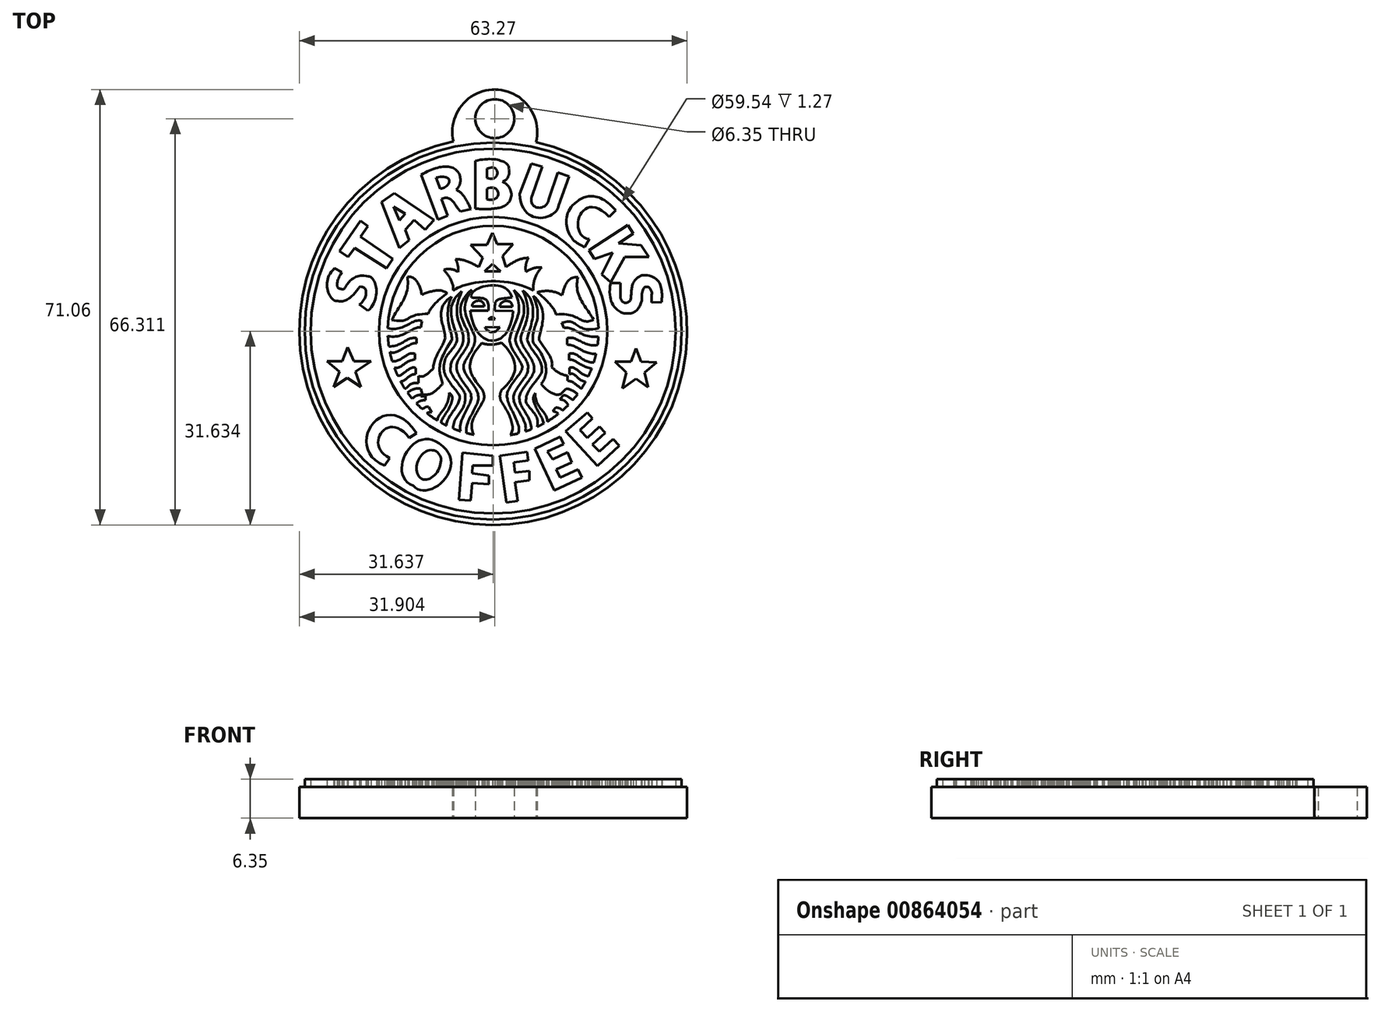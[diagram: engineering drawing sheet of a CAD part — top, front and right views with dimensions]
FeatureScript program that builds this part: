
annotation { "Feature Type Name" : "Feature", "Feature Type Description" : "" }
export const myFeature = defineFeature(function(context is Context, id is Id, definition is map)
    precondition{}
    {
        {
            var Q0;
            Q0=qCreatedBy(makeId("Top.planeOp"),FACE);
            var sketch = newSketch(context, id + "F0", { "sketchPlane" : qUnion([Q0])});
            skCircle(sketch, "E0", {"center": v(-23.32, 12.26) * mm, "radius": 31.63 * mm});
            skLineSegment(sketch, "E1", {"start": v(-49.23, 22.5) * mm, "end": v(-48.02, 21.88) * mm});
            skFitSpline(sketch, "E2", {"points": [v(-49.23, 22.5) * mm, v(-48.66, 17.2) * mm], "startDerivative": vector(-6.87, -5.81) * mm, "endDerivative": vector(4.33, 0.74) * mm});
            skFitSpline(sketch, "E3", {"points": [v(-48.66, 17.2) * mm, v(-45.1, 19.5) * mm], "startDerivative": vector(4.5, -1.36) * mm, "endDerivative": vector(2.1, 3) * mm});
            skFitSpline(sketch, "E4", {"points": [v(-45.1, 19.5) * mm, v(-45.13, 16.6) * mm], "startDerivative": vector(4.2, 0.7) * mm, "endDerivative": vector(-4.3, -3.4) * mm});
            skLineSegment(sketch, "E5", {"start": v(-45.13, 16.6) * mm, "end": v(-43.76, 15.6) * mm});
            skFitSpline(sketch, "E6", {"points": [v(-43.76, 15.6) * mm, v(-43.7, 21.17) * mm], "startDerivative": vector(7.2, 6.3) * mm, "endDerivative": vector(-3.4, -0.6) * mm});
            skFitSpline(sketch, "E7", {"points": [v(-43.7, 21.17) * mm, v(-47.7, 19.13) * mm], "startDerivative": vector(-8.2, 2.4) * mm, "endDerivative": vector(-1.1, -0.8) * mm});
            skFitSpline(sketch, "E8", {"points": [v(-47.7, 19.13) * mm, v(-48.02, 21.88) * mm], "startDerivative": vector(-3.7, -0.2) * mm, "endDerivative": vector(3.74, 6.44) * mm});
            skLineSegment(sketch, "E9", {"start": v(-45, 30.28) * mm, "end": v(-48.4, 25.33) * mm});
            skLineSegment(sketch, "E10", {"start": v(-48.4, 25.33) * mm, "end": v(-46.97, 24.36) * mm});
            skLineSegment(sketch, "E11", {"start": v(-46.97, 24.36) * mm, "end": v(-45.95, 25.84) * mm});
            skLineSegment(sketch, "E12", {"start": v(-45.95, 25.84) * mm, "end": v(-40.68, 22.54) * mm});
            skLineSegment(sketch, "E13", {"start": v(-40.68, 22.54) * mm, "end": v(-39.72, 24.08) * mm});
            skLineSegment(sketch, "E14", {"start": v(-39.72, 24.08) * mm, "end": v(-44.96, 27.68) * mm});
            skLineSegment(sketch, "E15", {"start": v(-44.96, 27.68) * mm, "end": v(-43.8, 29.38) * mm});
            skLineSegment(sketch, "E16", {"start": v(-43.8, 29.38) * mm, "end": v(-45, 30.28) * mm});
            skLineSegment(sketch, "E17", {"start": v(-41.53, 33.34) * mm, "end": v(-38.6, 25.8) * mm});
            skLineSegment(sketch, "E18", {"start": v(-38.6, 25.8) * mm, "end": v(-37.01, 27.08) * mm});
            skLineSegment(sketch, "E19", {"start": v(-37.65, 28.82) * mm, "end": v(-36.22, 30.41) * mm});
            skLineSegment(sketch, "E20", {"start": v(-36.22, 30.41) * mm, "end": v(-34.45, 28.82) * mm});
            skLineSegment(sketch, "E21", {"start": v(-34.45, 28.82) * mm, "end": v(-32.97, 30.41) * mm});
            skLineSegment(sketch, "E22", {"start": v(-32.97, 30.41) * mm, "end": v(-39.47, 34.77) * mm});
            skLineSegment(sketch, "E23", {"start": v(-39.47, 34.77) * mm, "end": v(-41.53, 33.34) * mm});
            skPoint(sketch, "E24.startSnap0", {"position": v(-36.22, 32.6) * mm});
            skLineSegment(sketch, "E25", {"start": v(-38.63, 30.33) * mm, "end": v(-39.6, 32.6) * mm});
            skLineSegment(sketch, "E26", {"start": v(-38.63, 30.33) * mm, "end": v(-37.65, 31.42) * mm});
            skLineSegment(sketch, "E27", {"start": v(-37.65, 31.42) * mm, "end": v(-39.6, 32.6) * mm});
            skLineSegment(sketch, "E28", {"start": v(-37.65, 28.82) * mm, "end": v(-37.01, 27.08) * mm});
            skLineSegment(sketch, "E29", {"start": v(-35.04, 37.8) * mm, "end": v(-32.34, 30.5) * mm});
            skLineSegment(sketch, "E30", {"start": v(-32.34, 30.5) * mm, "end": v(-30.76, 31.07) * mm});
            skLineSegment(sketch, "E31", {"start": v(-30.76, 31.07) * mm, "end": v(-31.77, 33.8) * mm});
            skLineSegment(sketch, "E32", {"start": v(-32.66, 37.31) * mm, "end": v(-31.94, 35.49) * mm});
            skFitSpline(sketch, "E33", {"points": [v(-32.66, 37.31) * mm, v(-31.94, 35.49) * mm], "startDerivative": vector(9.27, 2.15) * mm, "endDerivative": vector(-5.47, -0.96) * mm});
            skFitSpline(sketch, "E34", {"points": [v(-31.77, 33.8) * mm, v(-28.68, 31.8) * mm], "startDerivative": vector(4.9, 2.77) * mm, "endDerivative": vector(2.4, -2.4) * mm});
            skFitSpline(sketch, "E35", {"points": [v(-35.04, 37.8) * mm, v(-28.79, 37.8) * mm], "startDerivative": vector(7.44, 4.41) * mm, "endDerivative": vector(2.9, -6.2) * mm});
            skFitSpline(sketch, "E36", {"points": [v(-28.79, 37.8) * mm, v(-29.36, 35.36) * mm], "startDerivative": vector(0.8, -3.3) * mm, "endDerivative": vector(-2.1, -1.9) * mm});
            skLineSegment(sketch, "E37", {"start": v(-28.68, 31.8) * mm, "end": v(-26.96, 32.16) * mm});
            skFitSpline(sketch, "E38", {"points": [v(-26.96, 32.16) * mm, v(-29.36, 35.36) * mm], "startDerivative": vector(-1.7, 4) * mm, "endDerivative": vector(-3.5, 1.7) * mm});
            skLineSegment(sketch, "E39", {"start": v(-26.25, 40.04) * mm, "end": v(-26.25, 32.25) * mm});
            skLineSegment(sketch, "E40", {"start": v(-24.34, 38.76) * mm, "end": v(-24.34, 37.25) * mm});
            skLineSegment(sketch, "E41", {"start": v(-24.34, 35.5) * mm, "end": v(-24.34, 33.76) * mm});
            skFitSpline(sketch, "E42", {"points": [v(-24.34, 35.5) * mm, v(-24.34, 33.76) * mm], "startDerivative": vector(6.91, 2.83) * mm, "endDerivative": vector(-7.96, 1.88) * mm});
            skFitSpline(sketch, "E43", {"points": [v(-24.34, 38.76) * mm, v(-24.34, 37.25) * mm], "startDerivative": vector(6.84, 3.16) * mm, "endDerivative": vector(-6.91, 2.42) * mm});
            skFitSpline(sketch, "E44", {"points": [v(-26.25, 40.04) * mm, v(-20.75, 38.6) * mm], "startDerivative": vector(9.59, 2.4) * mm, "endDerivative": vector(-0.76, -4.03) * mm});
            skFitSpline(sketch, "E45", {"points": [v(-20.75, 38.6) * mm, v(-21.8, 36.7) * mm], "startDerivative": vector(0.6, -3.03) * mm, "endDerivative": vector(-2.03, -0.34) * mm});
            skFitSpline(sketch, "E46", {"points": [v(-21.8, 36.7) * mm, v(-22.39, 32.4) * mm], "startDerivative": vector(7.51, -4.5) * mm, "endDerivative": vector(-6, -0.8) * mm});
            skFitSpline(sketch, "E47", {"points": [v(-26.25, 32.25) * mm, v(-22.39, 32.4) * mm], "startDerivative": vector(4.38, -0.28) * mm, "endDerivative": vector(3.9, 0.8) * mm});
            skLineSegment(sketch, "E48", {"start": v(-15.3, 39.13) * mm, "end": v(-16.9, 34.55) * mm});
            skLineSegment(sketch, "E49", {"start": v(-12.75, 38.13) * mm, "end": v(-14.25, 33.85) * mm});
            skFitSpline(sketch, "E50", {"points": [v(-16.9, 34.55) * mm, v(-14.25, 33.85) * mm], "startDerivative": vector(-3.26, -7.5) * mm, "endDerivative": vector(0.73, 6.68) * mm});
            skLineSegment(sketch, "E51", {"start": v(-17.1, 39.6) * mm, "end": v(-19, 34.64) * mm});
            skLineSegment(sketch, "E52", {"start": v(-10.86, 37.62) * mm, "end": v(-12.66, 32.75) * mm});
            skFitSpline(sketch, "E53", {"points": [v(-19, 34.64) * mm, v(-12.66, 32.75) * mm], "startDerivative": vector(1, -16.93) * mm, "endDerivative": vector(0.4, 6.62) * mm});
            skLineSegment(sketch, "E54", {"start": v(-17.1, 39.6) * mm, "end": v(-15.3, 39.13) * mm});
            skLineSegment(sketch, "E55", {"start": v(-12.75, 38.13) * mm, "end": v(-10.9, 37.49) * mm});
            skLineSegment(sketch, "E56", {"start": v(-3.33, 32) * mm, "end": v(-4.37, 30.9) * mm});
            skLineSegment(sketch, "E57", {"start": v(-7.65, 27.3) * mm, "end": v(-8.42, 25.98) * mm});
            skFitSpline(sketch, "E58", {"points": [v(-3.33, 32) * mm, v(-9.68, 33.36) * mm], "startDerivative": vector(-7.07, 8.25) * mm, "endDerivative": vector(-4.71, -4.38) * mm});
            skFitSpline(sketch, "E59", {"points": [v(-9.68, 33.36) * mm, v(-9.68, 26.68) * mm], "startDerivative": vector(-8.75, -6.06) * mm, "endDerivative": vector(4.68, -2.86) * mm});
            skLineSegment(sketch, "E60", {"start": v(-9.68, 26.68) * mm, "end": v(-8.42, 25.98) * mm});
            skFitSpline(sketch, "E61", {"points": [v(-4.37, 30.9) * mm, v(-7.65, 27.3) * mm], "startDerivative": vector(-14.62, 14.86) * mm, "endDerivative": vector(10.77, -1) * mm});
            skLineSegment(sketch, "E62", {"start": v(-1.35, 29.58) * mm, "end": v(-7.68, 25.44) * mm});
            skLineSegment(sketch, "E63", {"start": v(-7.68, 25.44) * mm, "end": v(-6.78, 24.07) * mm});
            skLineSegment(sketch, "E64", {"start": v(-1.35, 29.58) * mm, "end": v(-0.44, 28.2) * mm});
            skLineSegment(sketch, "E65", {"start": v(-0.44, 28.2) * mm, "end": v(-2.87, 26.6) * mm});
            skLineSegment(sketch, "E66", {"start": v(-2.87, 26.6) * mm, "end": v(0.84, 26.3) * mm});
            skLineSegment(sketch, "E67", {"start": v(0.84, 26.3) * mm, "end": v(2.08, 24.4) * mm});
            skLineSegment(sketch, "E68", {"start": v(2.08, 24.4) * mm, "end": v(-1.86, 24.4) * mm});
            skLineSegment(sketch, "E69", {"start": v(-1.86, 24.4) * mm, "end": v(-4.15, 20.24) * mm});
            skLineSegment(sketch, "E70", {"start": v(-4.15, 20.24) * mm, "end": v(-5.6, 21.5) * mm});
            skLineSegment(sketch, "E71", {"start": v(-5.6, 21.5) * mm, "end": v(-3.81, 25.1) * mm});
            skLineSegment(sketch, "E72", {"start": v(-3.81, 25.1) * mm, "end": v(-6.78, 24.07) * mm});
            skFitSpline(sketch, "E73", {"points": [v(4.15, 16.98) * mm, v(0.96, 21.4) * mm], "startDerivative": vector(0.4, 4.2) * mm, "endDerivative": vector(-10.76, -0.62) * mm});
            skFitSpline(sketch, "E74", {"points": [v(0.96, 21.4) * mm, v(-0.93, 17.24) * mm], "startDerivative": vector(-6.23, -2.66) * mm, "endDerivative": vector(-0.96, -4.87) * mm});
            skFitSpline(sketch, "E75", {"points": [v(-0.93, 17.24) * mm, v(-2.57, 17.71) * mm], "startDerivative": vector(-2.15, -1.81) * mm, "endDerivative": vector(-0.8, 2.66) * mm});
            skLineSegment(sketch, "E76", {"start": v(-2.57, 17.71) * mm, "end": v(-2.57, 20.1) * mm});
            skLineSegment(sketch, "E77", {"start": v(-2.57, 20.1) * mm, "end": v(-4.15, 20.1) * mm});
            skFitSpline(sketch, "E78", {"points": [v(-4.15, 20.1) * mm, v(-1.47, 15.18) * mm], "startDerivative": vector(-2.44, -12.23) * mm, "endDerivative": vector(1.98, 0.74) * mm});
            skFitSpline(sketch, "E79", {"points": [v(-1.47, 15.18) * mm, v(0.94, 18.03) * mm], "startDerivative": vector(5.38, -0.85) * mm, "endDerivative": vector(-0.5, 2.89) * mm});
            skFitSpline(sketch, "E80", {"points": [v(0.94, 18.03) * mm, v(2.51, 18.03) * mm], "startDerivative": vector(0.11, 7.42) * mm, "endDerivative": vector(-1.25, -4.13) * mm});
            skLineSegment(sketch, "E81", {"start": v(2.51, 18.03) * mm, "end": v(2.51, 16.92) * mm});
            skLineSegment(sketch, "E82", {"start": v(2.51, 16.92) * mm, "end": v(4.15, 16.98) * mm});
            skLineSegment(sketch, "E83", {"start": v(0, 9.47) * mm, "end": v(-0.85, 7.3) * mm});
            skLineSegment(sketch, "E84", {"start": v(-0.85, 7.3) * mm, "end": v(-3.42, 7.3) * mm});
            skLineSegment(sketch, "E85", {"start": v(-3.42, 7.3) * mm, "end": v(-1.57, 5.48) * mm});
            skLineSegment(sketch, "E86", {"start": v(-1.57, 5.48) * mm, "end": v(-2.21, 2.93) * mm});
            skLineSegment(sketch, "E87", {"start": v(-2.21, 2.93) * mm, "end": v(0, 4.48) * mm});
            skLineSegment(sketch, "E88", {"start": v(0, 4.48) * mm, "end": v(1.98, 3.12) * mm});
            skLineSegment(sketch, "E89", {"start": v(1.98, 3.12) * mm, "end": v(1.4, 5.48) * mm});
            skLineSegment(sketch, "E90", {"start": v(1.4, 5.48) * mm, "end": v(3.36, 7.16) * mm});
            skLineSegment(sketch, "E91", {"start": v(3.36, 7.16) * mm, "end": v(0.8, 7.3) * mm});
            skLineSegment(sketch, "E92", {"start": v(0.8, 7.3) * mm, "end": v(0, 9.47) * mm});
            skLineSegment(sketch, "E93", {"start": v(-47.07, 9.66) * mm, "end": v(-47.93, 7.37) * mm});
            skLineSegment(sketch, "E94", {"start": v(-47.93, 7.37) * mm, "end": v(-50.42, 7.37) * mm});
            skLineSegment(sketch, "E95", {"start": v(-50.42, 7.37) * mm, "end": v(-48.4, 5.61) * mm});
            skLineSegment(sketch, "E96", {"start": v(-48.4, 5.61) * mm, "end": v(-49.37, 3.14) * mm});
            skLineSegment(sketch, "E97", {"start": v(-49.37, 3.14) * mm, "end": v(-47.12, 4.63) * mm});
            skLineSegment(sketch, "E98", {"start": v(-47.12, 4.63) * mm, "end": v(-44.9, 3.14) * mm});
            skLineSegment(sketch, "E99", {"start": v(-44.9, 3.14) * mm, "end": v(-45.78, 5.61) * mm});
            skLineSegment(sketch, "E100", {"start": v(-45.78, 5.61) * mm, "end": v(-43.27, 7.37) * mm});
            skLineSegment(sketch, "E101", {"start": v(-43.27, 7.37) * mm, "end": v(-46.06, 7.37) * mm});
            skLineSegment(sketch, "E102", {"start": v(-46.06, 7.37) * mm, "end": v(-47.07, 9.66) * mm});
            skFitSpline(sketch, "E103", {"points": [v(-35.8, -4.4) * mm, v(-41.04, -9.69) * mm], "startDerivative": vector(-16.2, 24.29) * mm, "endDerivative": vector(20.89, -8.4) * mm});
            skFitSpline(sketch, "E104", {"points": [v(-37.03, -5.14) * mm, v(-40.2, -8.46) * mm], "startDerivative": vector(-10.45, 14.02) * mm, "endDerivative": vector(12.95, -6.18) * mm});
            skLineSegment(sketch, "E105", {"start": v(-35.8, -4.4) * mm, "end": v(-37.03, -5.14) * mm});
            skLineSegment(sketch, "E106", {"start": v(-40.2, -8.46) * mm, "end": v(-41.04, -9.69) * mm});
            skFitSpline(sketch, "E107", {"points": [v(-32.16, -6.08) * mm, v(-36.34, -12.95) * mm], "startDerivative": vector(16.44, -10.89) * mm, "endDerivative": vector(-7.1, 9.07) * mm});
            skFitSpline(sketch, "E108", {"points": [v(-32.16, -6.08) * mm, v(-36.34, -12.95) * mm], "startDerivative": vector(-13.12, 9.58) * mm, "endDerivative": vector(13.48, -4.94) * mm});
            skFitSpline(sketch, "E109", {"points": [v(-32.66, -7.32) * mm, v(-35.23, -11.65) * mm], "startDerivative": vector(6.85, -4.03) * mm, "endDerivative": vector(-5.66, 4.74) * mm});
            skFitSpline(sketch, "E110", {"points": [v(-32.66, -7.32) * mm, v(-35.23, -11.65) * mm], "startDerivative": vector(-6.44, 3.03) * mm, "endDerivative": vector(5.06, -4.74) * mm});
            skLineSegment(sketch, "E111", {"start": v(-28.34, -7.57) * mm, "end": v(-28.87, -15.27) * mm});
            skLineSegment(sketch, "E112", {"start": v(-28.87, -15.27) * mm, "end": v(-26.97, -15.4) * mm});
            skLineSegment(sketch, "E113", {"start": v(-26.97, -15.4) * mm, "end": v(-26.77, -12.53) * mm});
            skLineSegment(sketch, "E114", {"start": v(-26.77, -12.53) * mm, "end": v(-23.98, -12.72) * mm});
            skLineSegment(sketch, "E115", {"start": v(-23.98, -12.72) * mm, "end": v(-23.98, -11.3) * mm});
            skLineSegment(sketch, "E116", {"start": v(-23.98, -11.3) * mm, "end": v(-26.77, -10.94) * mm});
            skLineSegment(sketch, "E117", {"start": v(-26.77, -10.94) * mm, "end": v(-26.68, -9.63) * mm});
            skLineSegment(sketch, "E118", {"start": v(-26.68, -9.63) * mm, "end": v(-23.38, -9.63) * mm});
            skLineSegment(sketch, "E119", {"start": v(-23.38, -9.63) * mm, "end": v(-23.38, -8.1) * mm});
            skLineSegment(sketch, "E120", {"start": v(-23.38, -8.1) * mm, "end": v(-28.34, -7.57) * mm});
            skLineSegment(sketch, "E121", {"start": v(-22.26, -8.06) * mm, "end": v(-21.15, -15.71) * mm});
            skLineSegment(sketch, "E122", {"start": v(-21.15, -15.71) * mm, "end": v(-19.3, -15.45) * mm});
            skLineSegment(sketch, "E123", {"start": v(-19.3, -15.45) * mm, "end": v(-19.74, -12.4) * mm});
            skLineSegment(sketch, "E124", {"start": v(-19.74, -12.4) * mm, "end": v(-17.42, -12.06) * mm});
            skLineSegment(sketch, "E125", {"start": v(-17.42, -12.06) * mm, "end": v(-17.42, -10.52) * mm});
            skLineSegment(sketch, "E126", {"start": v(-17.42, -10.52) * mm, "end": v(-19.74, -10.83) * mm});
            skLineSegment(sketch, "E127", {"start": v(-19.74, -10.83) * mm, "end": v(-19.96, -9.17) * mm});
            skLineSegment(sketch, "E128", {"start": v(-19.96, -9.17) * mm, "end": v(-17.61, -8.86) * mm});
            skLineSegment(sketch, "E129", {"start": v(-17.61, -8.86) * mm, "end": v(-17.8, -7.41) * mm});
            skLineSegment(sketch, "E130", {"start": v(-17.8, -7.41) * mm, "end": v(-22.26, -8.06) * mm});
            skLineSegment(sketch, "E131", {"start": v(-16.54, -6.93) * mm, "end": v(-13.37, -13.75) * mm});
            skLineSegment(sketch, "E132", {"start": v(-13.37, -13.75) * mm, "end": v(-8.86, -11.66) * mm});
            skLineSegment(sketch, "E133", {"start": v(-8.86, -11.66) * mm, "end": v(-9.48, -10.31) * mm});
            skLineSegment(sketch, "E134", {"start": v(-9.48, -10.31) * mm, "end": v(-12.39, -11.66) * mm});
            skLineSegment(sketch, "E135", {"start": v(-12.39, -11.66) * mm, "end": v(-13.01, -10.31) * mm});
            skLineSegment(sketch, "E136", {"start": v(-13.01, -10.31) * mm, "end": v(-10.46, -9.13) * mm});
            skLineSegment(sketch, "E137", {"start": v(-10.46, -9.13) * mm, "end": v(-11.2, -7.53) * mm});
            skLineSegment(sketch, "E138", {"start": v(-11.2, -7.53) * mm, "end": v(-13.62, -8.65) * mm});
            skLineSegment(sketch, "E139", {"start": v(-16.54, -6.93) * mm, "end": v(-12.36, -5) * mm});
            skLineSegment(sketch, "E140", {"start": v(-12.36, -5) * mm, "end": v(-11.82, -6.15) * mm});
            skLineSegment(sketch, "E141", {"start": v(-11.82, -6.15) * mm, "end": v(-14.46, -7.38) * mm});
            skLineSegment(sketch, "E142", {"start": v(-14.46, -7.38) * mm, "end": v(-13.62, -8.65) * mm});
            skLineSegment(sketch, "E143", {"start": v(-11.5, -4.1) * mm, "end": v(-6.3, -9.72) * mm});
            skLineSegment(sketch, "E144", {"start": v(-6.3, -9.72) * mm, "end": v(-2.73, -6.42) * mm});
            skLineSegment(sketch, "E145", {"start": v(-2.73, -6.42) * mm, "end": v(-3.74, -5.32) * mm});
            skLineSegment(sketch, "E146", {"start": v(-3.74, -5.32) * mm, "end": v(-6, -7.4) * mm});
            skLineSegment(sketch, "E147", {"start": v(-6, -7.4) * mm, "end": v(-7.1, -6.22) * mm});
            skLineSegment(sketch, "E148", {"start": v(-7.1, -6.22) * mm, "end": v(-5.05, -4.34) * mm});
            skLineSegment(sketch, "E149", {"start": v(-5.05, -4.34) * mm, "end": v(-6, -3.3) * mm});
            skLineSegment(sketch, "E150", {"start": v(-6, -3.3) * mm, "end": v(-7.98, -5.13) * mm});
            skLineSegment(sketch, "E151", {"start": v(-7.98, -5.13) * mm, "end": v(-9.13, -3.89) * mm});
            skLineSegment(sketch, "E152", {"start": v(-9.13, -3.89) * mm, "end": v(-7.1, -2) * mm});
            skLineSegment(sketch, "E153", {"start": v(-7.1, -2) * mm, "end": v(-7.98, -1.05) * mm});
            skLineSegment(sketch, "E154", {"start": v(-7.98, -1.05) * mm, "end": v(-11.5, -4.1) * mm});
            skLineSegment(sketch, "E155", {"start": v(-23.47, 28.32) * mm, "end": v(-22.68, 26.44) * mm});
            skLineSegment(sketch, "E156", {"start": v(-22.68, 26.44) * mm, "end": v(-20.07, 26.44) * mm});
            skLineSegment(sketch, "E157", {"start": v(-20.07, 26.44) * mm, "end": v(-21.78, 24.48) * mm});
            skLineSegment(sketch, "E158", {"start": v(-21.78, 24.48) * mm, "end": v(-21.23, 22.74) * mm});
            skLineSegment(sketch, "E159", {"start": v(-23.47, 23.2) * mm, "end": v(-22.09, 22.02) * mm});
            skLineSegment(sketch, "E160", {"start": v(-23.47, 23.2) * mm, "end": v(-24.72, 22.02) * mm});
            skLineSegment(sketch, "E161", {"start": v(-24.72, 22.02) * mm, "end": v(-22.09, 22.02) * mm});
            skLineSegment(sketch, "E162", {"start": v(-23.47, 28.32) * mm, "end": v(-24.3, 26.35) * mm});
            skLineSegment(sketch, "E163", {"start": v(-24.3, 26.35) * mm, "end": v(-26.99, 26.35) * mm});
            skLineSegment(sketch, "E164", {"start": v(-26.99, 26.35) * mm, "end": v(-25, 24.26) * mm});
            skLineSegment(sketch, "E165", {"start": v(-25, 24.26) * mm, "end": v(-25.67, 22.72) * mm});
            skFitSpline(sketch, "E166", {"points": [v(-29.83, 18.82) * mm, v(-16.77, 18.9) * mm], "startDerivative": vector(3.6, 3.92) * mm, "endDerivative": vector(14.42, -8.07) * mm});
            skFitSpline(sketch, "E167", {"points": [v(-31.37, 22.26) * mm, v(-29.83, 18.82) * mm], "startDerivative": vector(2.43, -2.5) * mm, "endDerivative": vector(-0.31, -4.08) * mm});
            skFitSpline(sketch, "E168", {"points": [v(-31.37, 22.26) * mm, v(-29.02, 21.92) * mm], "startDerivative": vector(1.49, 0.78) * mm, "endDerivative": vector(2.35, -1.57) * mm});
            skFitSpline(sketch, "E169", {"points": [v(-29.46, 24.01) * mm, v(-29.02, 21.92) * mm], "startDerivative": vector(0.94, -1.65) * mm, "endDerivative": vector(-0.16, -2.12) * mm});
            skFitSpline(sketch, "E170", {"points": [v(-29.46, 24.01) * mm, v(-25.67, 22.72) * mm], "startDerivative": vector(3.84, 0.08) * mm, "endDerivative": vector(3.7, -2.15) * mm});
            skFitSpline(sketch, "E171", {"points": [v(-16.77, 18.9) * mm, v(-15.4, 22.65) * mm], "startDerivative": vector(-0.2, 4.33) * mm, "endDerivative": vector(3.1, 3.33) * mm});
            skFitSpline(sketch, "E172", {"points": [v(-15.4, 22.65) * mm, v(-17.96, 21.96) * mm], "startDerivative": vector(-2.94, 0.22) * mm, "endDerivative": vector(-2.44, -1.55) * mm});
            skFitSpline(sketch, "E173", {"points": [v(-17.96, 21.96) * mm, v(-17.53, 24.22) * mm], "startDerivative": vector(-0.6, 2.66) * mm, "endDerivative": vector(0.94, 1.22) * mm});
            skFitSpline(sketch, "E174", {"points": [v(-21.23, 22.74) * mm, v(-17.53, 24.22) * mm], "startDerivative": vector(3.33, 2.09) * mm, "endDerivative": vector(4.54, 0) * mm});
            skFitSpline(sketch, "E175", {"points": [v(-26.9, 17.8) * mm, v(-20.26, 17.75) * mm], "startDerivative": vector(-0.96, 5.66) * mm, "endDerivative": vector(2.07, -9.89) * mm});
            skFitSpline(sketch, "E176", {"points": [v(-26.9, 17.8) * mm, v(-24.11, 15.61) * mm], "startDerivative": vector(3.9, -1.04) * mm, "endDerivative": vector(-0.88, -8.21) * mm});
            skFitSpline(sketch, "E177", {"points": [v(-24.67, 12.9) * mm, v(-22.25, 12.93) * mm], "startDerivative": vector(0.79, -1.9) * mm, "endDerivative": vector(2.57, 4.41) * mm});
            skLineSegment(sketch, "E178", {"start": v(-24.67, 12.9) * mm, "end": v(-22.25, 12.93) * mm});
            skLineSegment(sketch, "E179", {"start": v(-24.08, 14.18) * mm, "end": v(-23.01, 14.18) * mm});
            skFitSpline(sketch, "E180", {"points": [v(-24.08, 14.18) * mm, v(-23.01, 14.18) * mm], "startDerivative": vector(1.05, 1.37) * mm, "endDerivative": vector(0.9, -1.58) * mm});
            skFitSpline(sketch, "E181", {"points": [v(-27.04, 15.6) * mm, v(-20.08, 15.57) * mm], "startDerivative": vector(1.96, -19.15) * mm, "endDerivative": vector(1.4, 20.06) * mm});
            skLineSegment(sketch, "E182", {"start": v(-27.04, 15.6) * mm, "end": v(-24.11, 15.61) * mm});
            skFitSpline(sketch, "E183", {"points": [v(-20.26, 17.75) * mm, v(-23.08, 15.6) * mm], "startDerivative": vector(-8.3, -0.7) * mm, "endDerivative": vector(-0.17, -5.73) * mm});
            skLineSegment(sketch, "E184", {"start": v(-20.08, 15.57) * mm, "end": v(-23.08, 15.6) * mm});
            skFitSpline(sketch, "E185", {"points": [v(-22.22, 16.25) * mm, v(-20.18, 16.22) * mm], "startDerivative": vector(-0.62, 2.67) * mm, "endDerivative": vector(0.3, -4.87) * mm});
            skFitSpline(sketch, "E186", {"points": [v(-21.49, 16.25) * mm, v(-20.84, 16.22) * mm], "startDerivative": vector(0.05, 1.2) * mm, "endDerivative": vector(0.25, -1.82) * mm});
            skLineSegment(sketch, "E187", {"start": v(-22.22, 16.25) * mm, "end": v(-20.18, 16.22) * mm});
            skFitSpline(sketch, "E188", {"points": [v(-26.76, 16.3) * mm, v(-24.76, 16.3) * mm], "startDerivative": vector(-0.34, 3.08) * mm, "endDerivative": vector(0.14, -4.37) * mm});
            skFitSpline(sketch, "E189", {"points": [v(-26.08, 16.3) * mm, v(-25.29, 16.29) * mm], "startDerivative": vector(0.2, 1.39) * mm, "endDerivative": vector(0.4, -1.53) * mm});
            skLineSegment(sketch, "E190", {"start": v(-26.76, 16.3) * mm, "end": v(-24.76, 16.3) * mm});
            skFitSpline(sketch, "E191", {"points": [v(-25.15, 10.33) * mm, v(-21.97, 10.37) * mm], "startDerivative": vector(2.7, -1.14) * mm, "endDerivative": vector(3.03, 1.08) * mm});
            skFitSpline(sketch, "E192", {"points": [v(-21.97, 10.37) * mm, v(-21.97, 2.63) * mm], "startDerivative": vector(10.1, -9.77) * mm, "endDerivative": vector(-7.54, -6.67) * mm});
            skFitSpline(sketch, "E193", {"points": [v(-25.15, 10.33) * mm, v(-25.15, 2.79) * mm], "startDerivative": vector(-9.36, -10.5) * mm, "endDerivative": vector(6.06, -7.48) * mm});
            skFitSpline(sketch, "E194", {"points": [v(-25.15, 2.79) * mm, v(-25.15, 0.54) * mm], "startDerivative": vector(1.3, -2.11) * mm, "endDerivative": vector(-1.6, -1.9) * mm});
            skFitSpline(sketch, "E195", {"points": [v(-21.97, 2.63) * mm, v(-21.97, 0.73) * mm], "startDerivative": vector(-0.92, -1.93) * mm, "endDerivative": vector(1.02, -1.86) * mm});
            skFitSpline(sketch, "E196", {"points": [v(-25.15, 0.54) * mm, v(-26.48, -4.64) * mm], "startDerivative": vector(-3.25, -6.67) * mm, "endDerivative": vector(2.78, -6.34) * mm});
            skFitSpline(sketch, "E197", {"points": [v(-21.97, 0.73) * mm, v(-20.53, -4.7) * mm], "startDerivative": vector(3.67, -5.26) * mm, "endDerivative": vector(-3, -3.62) * mm});
            skFitSpline(sketch, "E198", {"points": [v(-37.3, 21.13) * mm, v(-39.87, 14.07) * mm], "startDerivative": vector(1.47, -9.46) * mm, "endDerivative": vector(-3.23, -6.85) * mm});
            skFitSpline(sketch, "E199", {"points": [v(-37.3, 21.13) * mm, v(-34.94, 18.24) * mm], "startDerivative": vector(4.3, 0.45) * mm, "endDerivative": vector(0.96, -4.3) * mm});
            skFitSpline(sketch, "E200", {"points": [v(-34.94, 18.24) * mm, v(-30.82, 18.46) * mm], "startDerivative": vector(4.64, 1.53) * mm, "endDerivative": vector(3.74, -2.72) * mm});
            skFitSpline(sketch, "E201", {"points": [v(-30.82, 18.46) * mm, v(-33.95, 15.09) * mm], "startDerivative": vector(-3.75, -2.78) * mm, "endDerivative": vector(-1.86, -4.12) * mm});
            skFitSpline(sketch, "E202", {"points": [v(-39.87, 14.07) * mm, v(-33.95, 15.09) * mm], "startDerivative": vector(10.28, -1.75) * mm, "endDerivative": vector(12.35, 0.11) * mm});
            skCircle(sketch, "E203", {"center": v(-23.32, 12.26) * mm, "radius": 18.62 * mm});
            skCircle(sketch, "E204", {"center": v(-23.32, 12.26) * mm, "radius": 17.2 * mm});
            skCircle(sketch, "E205", {"center": v(-23.32, 12.26) * mm, "radius": 30.76 * mm});
            skCircle(sketch, "E206", {"center": v(-23.32, 12.26) * mm, "radius": 29.77 * mm});
            skFitSpline(sketch, "E207", {"points": [v(-9.48, 21.06) * mm, v(-6.95, 14.16) * mm], "startDerivative": vector(-2.38, -8.84) * mm, "endDerivative": vector(3.62, -6.46) * mm});
            skFitSpline(sketch, "E208", {"points": [v(-9.48, 21.06) * mm, v(-12.09, 18.12) * mm], "startDerivative": vector(-6.23, 0.45) * mm, "endDerivative": vector(-1.13, -2.72) * mm});
            skFitSpline(sketch, "E209", {"points": [v(-16.12, 18.6) * mm, v(-12.09, 18.12) * mm], "startDerivative": vector(4.3, 1.25) * mm, "endDerivative": vector(3.51, -2.27) * mm});
            skFitSpline(sketch, "E210", {"points": [v(-16.12, 18.6) * mm, v(-13.06, 15) * mm], "startDerivative": vector(3.62, -2.83) * mm, "endDerivative": vector(0.45, -3.06) * mm});
            skFitSpline(sketch, "E211", {"points": [v(-13.06, 15) * mm, v(-6.95, 14.16) * mm], "startDerivative": vector(11.75, 1.2) * mm, "endDerivative": vector(6.07, 3.47) * mm});
            skFitSpline(sketch, "E212", {"points": [v(-34.93, 13.92) * mm, v(-40.5, 12.74) * mm], "startDerivative": vector(-4.63, 1.77) * mm, "endDerivative": vector(-7.71, 2.16) * mm});
            skLineSegment(sketch, "E213", {"start": v(-34.93, 13.92) * mm, "end": v(-35.15, 12.85) * mm});
            skFitSpline(sketch, "E214", {"points": [v(-35.15, 12.85) * mm, v(-40.5, 11.46) * mm], "startDerivative": vector(-3.32, 1.22) * mm, "endDerivative": vector(-7.72, 1.76) * mm});
            skFitSpline(sketch, "E215", {"points": [v(-35.8, 11.13) * mm, v(-40.33, 9.78) * mm], "startDerivative": vector(-5.26, 0.92) * mm, "endDerivative": vector(-7.25, -0.07) * mm});
            skLineSegment(sketch, "E216", {"start": v(-35.8, 11.13) * mm, "end": v(-35.8, 10.25) * mm});
            skFitSpline(sketch, "E217", {"points": [v(-35.8, 10.25) * mm, v(-40.17, 8.85) * mm], "startDerivative": vector(-2.2, 1.43) * mm, "endDerivative": vector(-3, 1.94) * mm});
            skLineSegment(sketch, "E218", {"start": v(-36.08, 8.57) * mm, "end": v(-36.08, 7.68) * mm});
            skFitSpline(sketch, "E219", {"points": [v(-36.08, 8.57) * mm, v(-39.8, 7.37) * mm], "startDerivative": vector(-3.58, 1.5) * mm, "endDerivative": vector(-4.24, 0.85) * mm});
            skFitSpline(sketch, "E220", {"points": [v(-36.08, 7.68) * mm, v(-39.43, 6.26) * mm], "startDerivative": vector(-5.93, -1.2) * mm, "endDerivative": vector(-4.56, 0.07) * mm});
            skLineSegment(sketch, "E221", {"start": v(-35.97, 6.22) * mm, "end": v(-35.97, 5.25) * mm});
            skFitSpline(sketch, "E222", {"points": [v(-35.97, 6.22) * mm, v(-38.92, 5.03) * mm], "startDerivative": vector(-2.6, 1.88) * mm, "endDerivative": vector(-1.78, 1.2) * mm});
            skFitSpline(sketch, "E223", {"points": [v(-35.97, 5.25) * mm, v(-38.44, 4.08) * mm], "startDerivative": vector(-3.93, -0.1) * mm, "endDerivative": vector(-2.76, 0.24) * mm});
            skFitSpline(sketch, "E224", {"points": [v(-35.51, 3.8) * mm, v(-37.75, 2.92) * mm], "startDerivative": vector(-5.28, 0.6) * mm, "endDerivative": vector(-1.62, 0.34) * mm});
            skFitSpline(sketch, "E225", {"points": [v(-35.11, 2.83) * mm, v(-37.26, 2.2) * mm], "startDerivative": vector(-1.97, 0.82) * mm, "endDerivative": vector(-1, -1.35) * mm});
            skLineSegment(sketch, "E226", {"start": v(-35.11, 2.83) * mm, "end": v(-34.88, 1.94) * mm});
            skFitSpline(sketch, "E227", {"points": [v(-34.88, 1.94) * mm, v(-31.55, 3.65) * mm], "startDerivative": vector(5.15, -1.1) * mm, "endDerivative": vector(2.57, 2.15) * mm});
            skLineSegment(sketch, "E228", {"start": v(-35.51, 3.8) * mm, "end": v(-35.51, 4.94) * mm});
            skFitSpline(sketch, "E229", {"points": [v(-35.51, 4.94) * mm, v(-33.06, 6.13) * mm], "startDerivative": vector(3.94, -1.13) * mm, "endDerivative": vector(2.03, 0.84) * mm});
            skFitSpline(sketch, "E230", {"points": [v(-33.06, 6.13) * mm, v(-31.14, 11.16) * mm], "startDerivative": vector(-0.5, 5.04) * mm, "endDerivative": vector(0.7, 3.82) * mm});
            skFitSpline(sketch, "E231", {"points": [v(-31.14, 11.16) * mm, v(-30.14, 17.92) * mm], "startDerivative": vector(-0.12, 6.25) * mm, "endDerivative": vector(9.14, 6.37) * mm});
            skFitSpline(sketch, "E232", {"points": [v(-31.55, 3.65) * mm, v(-30.16, 10.63) * mm], "startDerivative": vector(-1.63, 6.08) * mm, "endDerivative": vector(7.98, 12.11) * mm});
            skFitSpline(sketch, "E233", {"points": [v(-30.16, 10.63) * mm, v(-30.14, 17.92) * mm], "startDerivative": vector(1.93, 2.34) * mm, "endDerivative": vector(4.74, 11.4) * mm});
            skLineSegment(sketch, "E234", {"start": v(-35.1, 1.9) * mm, "end": v(-35.1, 1.63) * mm});
            skLineSegment(sketch, "E235", {"start": v(-35.1, 1.63) * mm, "end": v(-34.35, 1.63) * mm});
            skLineSegment(sketch, "E236", {"start": v(-34.35, 1.63) * mm, "end": v(-34.35, 1.02) * mm});
            skFitSpline(sketch, "E237", {"points": [v(-34.35, 1.02) * mm, v(-35.84, 0.48) * mm], "startDerivative": vector(-3.5, -0.24) * mm, "endDerivative": vector(-0.96, -0.52) * mm});
            skFitSpline(sketch, "E238", {"points": [v(-35.1, 1.9) * mm, v(-36.5, 1.23) * mm], "startDerivative": vector(-1.5, -0.05) * mm, "endDerivative": vector(-1.12, -1.26) * mm});
            skFitSpline(sketch, "E239", {"points": [v(-33.87, -0.05) * mm, v(-34.95, -0.4) * mm], "startDerivative": vector(-1.69, 0.16) * mm, "endDerivative": vector(-1.56, -0.23) * mm});
            skLineSegment(sketch, "E240.bottom", {"start": v(-33.87, -0.05) * mm, "end": v(-33.95, -0.1) * mm});
            skLineSegment(sketch, "E241", {"start": v(-33.87, -0.05) * mm, "end": v(-33.36, -0.95) * mm});
            skFitSpline(sketch, "E242", {"points": [v(-33.36, -0.95) * mm, v(-34.11, -1.12) * mm], "startDerivative": vector(-0.52, -0.07) * mm, "endDerivative": vector(-0.08, -0.42) * mm});
            skFitSpline(sketch, "E243", {"points": [v(-30.48, 2.2) * mm, v(-32.4, -2.33) * mm], "startDerivative": vector(-0.4, -8.5) * mm, "endDerivative": vector(0.1, -3.7) * mm});
            skFitSpline(sketch, "E244", {"points": [v(-30.48, 2.2) * mm, v(-31.75, -2.72) * mm], "startDerivative": vector(5.27, -3.57) * mm, "endDerivative": vector(1.41, -1.58) * mm});
            skLineSegment(sketch, "E245", {"start": v(-12.11, 13.62) * mm, "end": v(-11.75, 12.76) * mm});
            skFitSpline(sketch, "E246", {"points": [v(-12.11, 13.62) * mm, v(-6.14, 12.75) * mm], "startDerivative": vector(7.88, 3.03) * mm, "endDerivative": vector(11.38, 2.91) * mm});
            skFitSpline(sketch, "E247", {"points": [v(-11.75, 12.76) * mm, v(-6.16, 11.34) * mm], "startDerivative": vector(5.46, 1.08) * mm, "endDerivative": vector(9.44, 0.65) * mm});
            skFitSpline(sketch, "E248", {"points": [v(-11.26, 11.1) * mm, v(-6.28, 10) * mm], "startDerivative": vector(4.31, 1.62) * mm, "endDerivative": vector(6.3, 1.36) * mm});
            skLineSegment(sketch, "E249", {"start": v(-11.26, 11.1) * mm, "end": v(-11.26, 10.07) * mm});
            skFitSpline(sketch, "E250", {"points": [v(-11.26, 10.07) * mm, v(-6.54, 8.53) * mm], "startDerivative": vector(6.26, -0.67) * mm, "endDerivative": vector(7.41, -0.3) * mm});
            skLineSegment(sketch, "E251", {"start": v(-10.94, 8.54) * mm, "end": v(-10.94, 7.55) * mm});
            skFitSpline(sketch, "E252", {"points": [v(-10.94, 8.54) * mm, v(-6.9, 7.2) * mm], "startDerivative": vector(4.45, 1.58) * mm, "endDerivative": vector(5.92, 0.7) * mm});
            skFitSpline(sketch, "E253", {"points": [v(-10.94, 7.55) * mm, v(-7.25, 6.17) * mm], "startDerivative": vector(2.2, 1.2) * mm, "endDerivative": vector(5.41, -0.72) * mm});
            skLineSegment(sketch, "E254", {"start": v(-10.84, 6.28) * mm, "end": v(-10.84, 5.26) * mm});
            skFitSpline(sketch, "E255", {"points": [v(-10.84, 6.28) * mm, v(-7.79, 4.9) * mm], "startDerivative": vector(3.33, 1.16) * mm, "endDerivative": vector(4.27, -0.5) * mm});
            skFitSpline(sketch, "E256", {"points": [v(-10.84, 5.26) * mm, v(-8.25, 4) * mm], "startDerivative": vector(3.13, 0.88) * mm, "endDerivative": vector(4.71, -1.14) * mm});
            skFitSpline(sketch, "E257", {"points": [v(-8.9, 2.92) * mm, v(-11.18, 4.18) * mm], "startDerivative": vector(-1.1, 0.2) * mm, "endDerivative": vector(-2.89, 0.1) * mm});
            skLineSegment(sketch, "E258", {"start": v(-11.18, 4.18) * mm, "end": v(-11.18, 4.98) * mm});
            skFitSpline(sketch, "E259", {"points": [v(-11.18, 4.98) * mm, v(-13.8, 6.42) * mm], "startDerivative": vector(-3.94, 0.77) * mm, "endDerivative": vector(-2.21, 2.02) * mm});
            skFitSpline(sketch, "E260", {"points": [v(-13.8, 6.42) * mm, v(-15.77, 10.7) * mm], "startDerivative": vector(1.7, 3.41) * mm, "endDerivative": vector(-2.72, 4.37) * mm});
            skFitSpline(sketch, "E261", {"points": [v(-15.77, 10.7) * mm, v(-16.79, 18.03) * mm], "startDerivative": vector(-1.18, 3.07) * mm, "endDerivative": vector(-9.33, 8.15) * mm});
            skFitSpline(sketch, "E262", {"points": [v(-16.79, 18.03) * mm, v(-16.79, 10.32) * mm], "startDerivative": vector(5.79, -12.52) * mm, "endDerivative": vector(1.65, -8.62) * mm});
            skFitSpline(sketch, "E263", {"points": [v(-16.79, 10.32) * mm, v(-15.49, 3.7) * mm], "startDerivative": vector(7.32, -7.56) * mm, "endDerivative": vector(-3.9, -3.9) * mm});
            skFitSpline(sketch, "E264", {"points": [v(-15.49, 3.7) * mm, v(-12.26, 2.05) * mm], "startDerivative": vector(1.89, -2.95) * mm, "endDerivative": vector(2.36, 1.89) * mm});
            skLineSegment(sketch, "E265", {"start": v(-12.26, 2.05) * mm, "end": v(-11.6, 2.72) * mm});
            skFitSpline(sketch, "E266", {"points": [v(-11.6, 2.72) * mm, v(-9.55, 1.97) * mm], "startDerivative": vector(1.18, 1.54) * mm, "endDerivative": vector(1.16, -0.93) * mm});
            skLineSegment(sketch, "E267", {"start": v(-12.45, 1.16) * mm, "end": v(-11.82, 1.84) * mm});
            skFitSpline(sketch, "E268", {"points": [v(-11.82, 1.84) * mm, v(-10.34, 1) * mm], "startDerivative": vector(1.69, -0.3) * mm, "endDerivative": vector(1.08, -1.07) * mm});
            skFitSpline(sketch, "E269", {"points": [v(-12.45, 1.16) * mm, v(-11.08, 0.2) * mm], "startDerivative": vector(2.63, -0.35) * mm, "endDerivative": vector(0.58, -1.11) * mm});
            skLineSegment(sketch, "E270", {"start": v(-13.06, -0.22) * mm, "end": v(-13.6, -0.76) * mm});
            skFitSpline(sketch, "E271", {"points": [v(-13.06, -0.22) * mm, v(-12.07, -0.73) * mm], "startDerivative": vector(1.54, 0) * mm, "endDerivative": vector(0.2, -0.96) * mm});
            skFitSpline(sketch, "E272", {"points": [v(-13.6, -0.76) * mm, v(-12.69, -1.24) * mm], "startDerivative": vector(1.14, -0.5) * mm, "endDerivative": vector(0.74, -0.9) * mm});
            skFitSpline(sketch, "E273", {"points": [v(-16.44, 2.13) * mm, v(-14.5, -2.49) * mm], "startDerivative": vector(-0.65, -6.4) * mm, "endDerivative": vector(-0.62, -4.04) * mm});
            skFitSpline(sketch, "E274", {"points": [v(-16.44, 2.13) * mm, v(-15.09, -2.83) * mm], "startDerivative": vector(-3.48, -4.07) * mm, "endDerivative": vector(0.4, -4.45) * mm});
            skFitSpline(sketch, "E275", {"points": [v(-16.16, -3.36) * mm, v(-17.94, 1.21) * mm], "startDerivative": vector(2.09, 6.74) * mm, "endDerivative": vector(1.47, 3.64) * mm});
            skFitSpline(sketch, "E276", {"points": [v(-17.94, 1.21) * mm, v(-15.38, 5.9) * mm], "startDerivative": vector(-0.09, 4.92) * mm, "endDerivative": vector(-0.43, 2.94) * mm});
            skFitSpline(sketch, "E277", {"points": [v(-15.38, 5.9) * mm, v(-17.8, 10.87) * mm], "startDerivative": vector(0.02, 6.48) * mm, "endDerivative": vector(-2.67, 7.08) * mm});
            skFitSpline(sketch, "E278", {"points": [v(-17.8, 10.87) * mm, v(-18.48, 18.9) * mm], "startDerivative": vector(1.23, 5.75) * mm, "endDerivative": vector(-9.14, 6.57) * mm});
            skFitSpline(sketch, "E279", {"points": [v(-18.48, 18.9) * mm, v(-18.8, 10.94) * mm], "startDerivative": vector(6.16, -13.04) * mm, "endDerivative": vector(0.41, -4.61) * mm});
            skFitSpline(sketch, "E280", {"points": [v(-18.8, 10.94) * mm, v(-16.65, 5.88) * mm], "startDerivative": vector(-0.14, -3.87) * mm, "endDerivative": vector(-1.03, -4.93) * mm});
            skFitSpline(sketch, "E281", {"points": [v(-16.65, 5.88) * mm, v(-19.05, 1.26) * mm], "startDerivative": vector(-0.2, -3.7) * mm, "endDerivative": vector(0.62, -3.6) * mm});
            skFitSpline(sketch, "E282", {"points": [v(-19.05, 1.26) * mm, v(-17.07, -3.75) * mm], "startDerivative": vector(0.3, -5.34) * mm, "endDerivative": vector(0.48, -7.34) * mm});
            skFitSpline(sketch, "E283", {"points": [v(-18.05, -4.1) * mm, v(-20, 1.42) * mm], "startDerivative": vector(1.25, 5.84) * mm, "endDerivative": vector(0.43, 4.25) * mm});
            skFitSpline(sketch, "E284", {"points": [v(-20, 1.42) * mm, v(-17.67, 6.08) * mm], "startDerivative": vector(0, 4.66) * mm, "endDerivative": vector(-0.35, 3.97) * mm});
            skFitSpline(sketch, "E285", {"points": [v(-17.67, 6.08) * mm, v(-19.7, 10.96) * mm], "startDerivative": vector(1.51, 3.93) * mm, "endDerivative": vector(0, 5.1) * mm});
            skFitSpline(sketch, "E286", {"points": [v(-19.7, 10.96) * mm, v(-19.97, 18.96) * mm], "startDerivative": vector(0.62, 5.58) * mm, "endDerivative": vector(-10.6, 8.2) * mm});
            skFitSpline(sketch, "E287", {"points": [v(-19.97, 18.96) * mm, v(-20.6, 11.1) * mm], "startDerivative": vector(6.32, -10.6) * mm, "endDerivative": vector(-1.3, -7.26) * mm});
            skFitSpline(sketch, "E288", {"points": [v(-20.6, 11.1) * mm, v(-18.6, 6.2) * mm], "startDerivative": vector(-1.08, -4.6) * mm, "endDerivative": vector(-0.94, -2.77) * mm});
            skFitSpline(sketch, "E289", {"points": [v(-18.6, 6.2) * mm, v(-21.02, 1.4) * mm], "startDerivative": vector(-0.53, -3.2) * mm, "endDerivative": vector(1.47, -4.23) * mm});
            skFitSpline(sketch, "E290", {"points": [v(-21.02, 1.4) * mm, v(-19.24, -4.44) * mm], "startDerivative": vector(0.3, -4.17) * mm, "endDerivative": vector(-2.23, -3.71) * mm});
            skFitSpline(sketch, "E291", {"points": [v(-30.93, -3.15) * mm, v(-28.8, 1.45) * mm], "startDerivative": vector(-0.48, 4.07) * mm, "endDerivative": vector(-0.1, 4.36) * mm});
            skFitSpline(sketch, "E292", {"points": [v(-28.8, 1.45) * mm, v(-31.36, 6.35) * mm], "startDerivative": vector(0.82, 1.95) * mm, "endDerivative": vector(0.62, 5.75) * mm});
            skFitSpline(sketch, "E293", {"points": [v(-31.36, 6.35) * mm, v(-29.27, 11.35) * mm], "startDerivative": vector(-0.33, 7.6) * mm, "endDerivative": vector(-1.38, 5.37) * mm});
            skFitSpline(sketch, "E294", {"points": [v(-29.27, 11.35) * mm, v(-28.43, 18.76) * mm], "startDerivative": vector(-0.61, 5.02) * mm, "endDerivative": vector(9.8, 7.48) * mm});
            skFitSpline(sketch, "E295", {"points": [v(-28.43, 18.76) * mm, v(-28.21, 11.35) * mm], "startDerivative": vector(-5.95, -12.2) * mm, "endDerivative": vector(-0.14, -4.78) * mm});
            skFitSpline(sketch, "E296", {"points": [v(-28.21, 11.35) * mm, v(-30.27, 6.45) * mm], "startDerivative": vector(1.2, -5.57) * mm, "endDerivative": vector(0.33, -4.3) * mm});
            skFitSpline(sketch, "E297", {"points": [v(-30.27, 6.45) * mm, v(-27.9, 1.47) * mm], "startDerivative": vector(-1.47, -4.65) * mm, "endDerivative": vector(-1.49, -3.34) * mm});
            skFitSpline(sketch, "E298", {"points": [v(-27.9, 1.47) * mm, v(-29.88, -3.63) * mm], "startDerivative": vector(0.69, -6.76) * mm, "endDerivative": vector(-0.16, -7) * mm});
            skFitSpline(sketch, "E299", {"points": [v(-27.67, -4.37) * mm, v(-25.75, 1.56) * mm], "startDerivative": vector(-1.09, 6.32) * mm, "endDerivative": vector(-0.7, 4.68) * mm});
            skFitSpline(sketch, "E300", {"points": [v(-25.75, 1.56) * mm, v(-28.15, 6.53) * mm], "startDerivative": vector(-0.09, 5) * mm, "endDerivative": vector(0.53, 4.2) * mm});
            skFitSpline(sketch, "E301", {"points": [v(-28.15, 6.53) * mm, v(-26.3, 11.26) * mm], "startDerivative": vector(-0.58, 2.43) * mm, "endDerivative": vector(-1.03, 5.16) * mm});
            skFitSpline(sketch, "E302", {"points": [v(-26.3, 11.26) * mm, v(-26.8, 19.06) * mm], "startDerivative": vector(-1.5, 6.36) * mm, "endDerivative": vector(7.68, 10.72) * mm});
            skFitSpline(sketch, "E303", {"points": [v(-26.8, 19.06) * mm, v(-27.36, 11.21) * mm], "startDerivative": vector(-12.08, -10.78) * mm, "endDerivative": vector(-1.11, -5.26) * mm});
            skFitSpline(sketch, "E304", {"points": [v(-27.36, 11.21) * mm, v(-29.3, 6.29) * mm], "startDerivative": vector(1.42, -5.35) * mm, "endDerivative": vector(0.52, -5.3) * mm});
            skFitSpline(sketch, "E305", {"points": [v(-29.3, 6.29) * mm, v(-26.92, 1.61) * mm], "startDerivative": vector(0.36, -5.35) * mm, "endDerivative": vector(-0.72, -2.57) * mm});
            skFitSpline(sketch, "E306", {"points": [v(-26.92, 1.61) * mm, v(-28.68, -4.07) * mm], "startDerivative": vector(0.96, -3.83) * mm, "endDerivative": vector(1.14, -6.53) * mm});
            skArc(sketch, "E307", {"start": v(-16.33, 43.11) * mm, "mid": v(-23, 51.69) * mm, "end": v(-29.8, 43.23) * mm});
            skPoint(sketch, "E308", {"position": v(-23.06, 46.94) * mm});
            skSolve(sketch);
        }
        {
            var Q0;
            Q0=makeQuery(id+"F0.imprint","IMPRINT",FACE,{"disambiguationData":[TD([[makeQuery(id+"F0.imprint","IMPRINT",EDGE,{"derivedFrom":sQuery(id+"F0.wireOp",EDGE,"E198")}),1.0]])]});
            var Q1;
            {var subQ0=sQuery(id+"F0.wireOp",EDGE,"E212");Q1=makeQuery(id+"F0.imprint","IMPRINT",FACE,{"disambiguationData":[TD([[makeQuery(id+"F0.imprint","IMPRINT",EDGE,{"derivedFrom":subQ0}),1.0]])]});}
            var Q2;
            {var subQ0=sQuery(id+"F0.wireOp",EDGE,"E215");Q2=makeQuery(id+"F0.imprint","IMPRINT",FACE,{"disambiguationData":[TD([[makeQuery(id+"F0.imprint","IMPRINT",EDGE,{"derivedFrom":subQ0}),1.0]])]});}
            var Q3;
            Q3=makeQuery(id+"F0.imprint","IMPRINT",FACE,{"disambiguationData":[TD([[makeQuery(id+"F0.imprint","IMPRINT",EDGE,{"derivedFrom":sQuery(id+"F0.wireOp",EDGE,"E218")}),-1.0]])]});
            var Q4;
            Q4=makeQuery(id+"F0.imprint","IMPRINT",FACE,{"disambiguationData":[TD([[makeQuery(id+"F0.imprint","IMPRINT",EDGE,{"derivedFrom":sQuery(id+"F0.wireOp",EDGE,"E221")}),-1.0]])]});
            var Q5;
            {var subQ0=sQuery(id+"F0.wireOp",EDGE,"E224");Q5=makeQuery(id+"F0.imprint","IMPRINT",FACE,{"disambiguationData":[TD([[makeQuery(id+"F0.imprint","IMPRINT",EDGE,{"derivedFrom":subQ0}),1.0]])]});}
            var Q6;
            Q6=makeQuery(id+"F0.imprint","IMPRINT",FACE,{"disambiguationData":[TD([[makeQuery(id+"F0.imprint","IMPRINT",EDGE,{"derivedFrom":sQuery(id+"F0.wireOp",EDGE,"E234")}),-1.0]])]});
            var Q7;
            {var subQ0=sQuery(id+"F0.wireOp",EDGE,"E239");Q7=makeQuery(id+"F0.imprint","IMPRINT",FACE,{"disambiguationData":[TD([[makeQuery(id+"F0.imprint","IMPRINT",EDGE,{"derivedFrom":subQ0}),1.0]])]});}
            var Q8;
            {var subQ0=sQuery(id+"F0.wireOp",EDGE,"E243");Q8=makeQuery(id+"F0.imprint","IMPRINT",FACE,{"disambiguationData":[TD([[makeQuery(id+"F0.imprint","IMPRINT",EDGE,{"derivedFrom":subQ0}),1.0]])]});}
            var Q9;
            {var subQ0=sQuery(id+"F0.wireOp",EDGE,"E291");Q9=makeQuery(id+"F0.imprint","IMPRINT",FACE,{"disambiguationData":[TD([[makeQuery(id+"F0.imprint","IMPRINT",EDGE,{"derivedFrom":subQ0}),-1.0]])]});}
            var Q10;
            {var subQ0=sQuery(id+"F0.wireOp",EDGE,"E299");Q10=makeQuery(id+"F0.imprint","IMPRINT",FACE,{"disambiguationData":[TD([[makeQuery(id+"F0.imprint","IMPRINT",EDGE,{"derivedFrom":subQ0}),1.0]])]});}
            var Q11;
            Q11=makeQuery(id+"F0.imprint","IMPRINT",FACE,{"disambiguationData":[TD([[makeQuery(id+"F0.imprint","IMPRINT",EDGE,{"derivedFrom":sQuery(id+"F0.wireOp",EDGE,"E155")}),-1.0]])]});
            var Q12;
            Q12=makeQuery(id+"F0.imprint","IMPRINT",FACE,{"disambiguationData":[TD([[makeQuery(id+"F0.imprint","IMPRINT",EDGE,{"derivedFrom":sQuery(id+"F0.wireOp",EDGE,"E175")}),-1.0]])]});
            var Q13;
            {var subQ0=sQuery(id+"F0.wireOp",EDGE,"E185");Q13=makeQuery(id+"F0.imprint","IMPRINT",FACE,{"disambiguationData":[TD([[makeQuery(id+"F0.imprint","IMPRINT",EDGE,{"derivedFrom":subQ0}),-1.0]])]});}
            var Q14;
            {var subQ0=sQuery(id+"F0.wireOp",EDGE,"E190");var subQ1=sQuery(id+"F0.wireOp",EDGE,"E189");var subQ2=makeQuery(id+"F0.imprint","INTERSECT",VERTEX,{"disambiguationData":[OD(0.0)],"derivedFrom":[subQ1,subQ0]});Q14=makeQuery(id+"F0.imprint","IMPRINT",FACE,{"disambiguationData":[TD([[makeQuery(id+"F0.imprint","IMPRINT",EDGE,{"disambiguationData":[TD([[subQ2,-1.0]])],"derivedFrom":subQ1}),-1.0]])]});}
            var Q15;
            {var subQ0=sQuery(id+"F0.wireOp",EDGE,"E188");Q15=makeQuery(id+"F0.imprint","IMPRINT",FACE,{"disambiguationData":[TD([[makeQuery(id+"F0.imprint","IMPRINT",EDGE,{"derivedFrom":subQ0}),-1.0]])]});}
            var Q16;
            Q16=makeQuery(id+"F0.imprint","IMPRINT",FACE,{"disambiguationData":[TD([[makeQuery(id+"F0.imprint","IMPRINT",EDGE,{"derivedFrom":sQuery(id+"F0.wireOp",EDGE,"E191")}),-1.0]])]});
            var Q17;
            {var subQ0=sQuery(id+"F0.wireOp",EDGE,"E283");Q17=makeQuery(id+"F0.imprint","IMPRINT",FACE,{"disambiguationData":[TD([[makeQuery(id+"F0.imprint","IMPRINT",EDGE,{"derivedFrom":subQ0}),1.0]])]});}
            var Q18;
            {var subQ0=sQuery(id+"F0.wireOp",EDGE,"E275");Q18=makeQuery(id+"F0.imprint","IMPRINT",FACE,{"disambiguationData":[TD([[makeQuery(id+"F0.imprint","IMPRINT",EDGE,{"derivedFrom":subQ0}),1.0]])]});}
            var Q19;
            {var subQ0=sQuery(id+"F0.wireOp",EDGE,"E273");Q19=makeQuery(id+"F0.imprint","IMPRINT",FACE,{"disambiguationData":[TD([[makeQuery(id+"F0.imprint","IMPRINT",EDGE,{"derivedFrom":subQ0}),-1.0]])]});}
            var Q20;
            Q20=makeQuery(id+"F0.imprint","IMPRINT",FACE,{"disambiguationData":[TD([[makeQuery(id+"F0.imprint","IMPRINT",EDGE,{"derivedFrom":sQuery(id+"F0.wireOp",EDGE,"E270")}),1.0]])]});
            var Q21;
            Q21=makeQuery(id+"F0.imprint","IMPRINT",FACE,{"disambiguationData":[TD([[makeQuery(id+"F0.imprint","IMPRINT",EDGE,{"derivedFrom":sQuery(id+"F0.wireOp",EDGE,"E267")}),-1.0]])]});
            var Q22;
            Q22=makeQuery(id+"F0.imprint","IMPRINT",FACE,{"disambiguationData":[TD([[makeQuery(id+"F0.imprint","IMPRINT",EDGE,{"derivedFrom":sQuery(id+"F0.wireOp",EDGE,"E254")}),1.0]])]});
            var Q23;
            {var subQ0=sQuery(id+"F0.wireOp",EDGE,"E257");Q23=makeQuery(id+"F0.imprint","IMPRINT",FACE,{"disambiguationData":[TD([[makeQuery(id+"F0.imprint","IMPRINT",EDGE,{"derivedFrom":subQ0}),1.0]])]});}
            var Q24;
            Q24=makeQuery(id+"F0.imprint","IMPRINT",FACE,{"disambiguationData":[TD([[makeQuery(id+"F0.imprint","IMPRINT",EDGE,{"derivedFrom":sQuery(id+"F0.wireOp",EDGE,"E251")}),1.0]])]});
            var Q25;
            {var subQ0=sQuery(id+"F0.wireOp",EDGE,"E248");Q25=makeQuery(id+"F0.imprint","IMPRINT",FACE,{"disambiguationData":[TD([[makeQuery(id+"F0.imprint","IMPRINT",EDGE,{"derivedFrom":subQ0}),-1.0]])]});}
            var Q26;
            Q26=makeQuery(id+"F0.imprint","IMPRINT",FACE,{"disambiguationData":[TD([[makeQuery(id+"F0.imprint","IMPRINT",EDGE,{"derivedFrom":sQuery(id+"F0.wireOp",EDGE,"E245")}),1.0]])]});
            var Q27;
            Q27=makeQuery(id+"F0.imprint","IMPRINT",FACE,{"disambiguationData":[TD([[makeQuery(id+"F0.imprint","IMPRINT",EDGE,{"derivedFrom":sQuery(id+"F0.wireOp",EDGE,"E207")}),-1.0]])]});
            var Q28;
            Q28=makeQuery(id+"F0.imprint","IMPRINT",FACE,{"disambiguationData":[TD([[makeQuery(id+"F0.imprint","IMPRINT",EDGE,{"derivedFrom":sQuery(id+"F0.wireOp",EDGE,"E1")}),-1.0]])]});
            var Q29;
            Q29=makeQuery(id+"F0.imprint","IMPRINT",FACE,{"disambiguationData":[TD([[makeQuery(id+"F0.imprint","IMPRINT",EDGE,{"derivedFrom":sQuery(id+"F0.wireOp",EDGE,"E9")}),1.0]])]});
            var Q30;
            Q30=makeQuery(id+"F0.imprint","IMPRINT",FACE,{"disambiguationData":[TD([[makeQuery(id+"F0.imprint","IMPRINT",EDGE,{"derivedFrom":sQuery(id+"F0.wireOp",EDGE,"E17")}),1.0]])]});
            var Q31;
            Q31=makeQuery(id+"F0.imprint","IMPRINT",FACE,{"disambiguationData":[TD([[makeQuery(id+"F0.imprint","IMPRINT",EDGE,{"derivedFrom":sQuery(id+"F0.wireOp",EDGE,"E29")}),1.0]])]});
            var Q32;
            Q32=makeQuery(id+"F0.imprint","IMPRINT",FACE,{"disambiguationData":[TD([[makeQuery(id+"F0.imprint","IMPRINT",EDGE,{"derivedFrom":sQuery(id+"F0.wireOp",EDGE,"E39")}),1.0]])]});
            var Q33;
            Q33=makeQuery(id+"F0.imprint","IMPRINT",FACE,{"disambiguationData":[TD([[makeQuery(id+"F0.imprint","IMPRINT",EDGE,{"derivedFrom":sQuery(id+"F0.wireOp",EDGE,"E48")}),-1.0]])]});
            var Q34;
            Q34=makeQuery(id+"F0.imprint","IMPRINT",FACE,{"disambiguationData":[TD([[makeQuery(id+"F0.imprint","IMPRINT",EDGE,{"derivedFrom":sQuery(id+"F0.wireOp",EDGE,"E56")}),-1.0]])]});
            var Q35;
            Q35=makeQuery(id+"F0.imprint","IMPRINT",FACE,{"disambiguationData":[TD([[makeQuery(id+"F0.imprint","IMPRINT",EDGE,{"derivedFrom":sQuery(id+"F0.wireOp",EDGE,"E62")}),1.0]])]});
            var Q36;
            Q36=makeQuery(id+"F0.imprint","IMPRINT",FACE,{"disambiguationData":[TD([[makeQuery(id+"F0.imprint","IMPRINT",EDGE,{"derivedFrom":sQuery(id+"F0.wireOp",EDGE,"E73")}),1.0]])]});
            var Q37;
            Q37=makeQuery(id+"F0.imprint","IMPRINT",FACE,{"disambiguationData":[TD([[makeQuery(id+"F0.imprint","IMPRINT",EDGE,{"derivedFrom":sQuery(id+"F0.wireOp",EDGE,"E83")}),1.0]])]});
            var Q38;
            Q38=makeQuery(id+"F0.imprint","IMPRINT",FACE,{"disambiguationData":[TD([[makeQuery(id+"F0.imprint","IMPRINT",EDGE,{"derivedFrom":sQuery(id+"F0.wireOp",EDGE,"E143")}),1.0]])]});
            var Q39;
            Q39=makeQuery(id+"F0.imprint","IMPRINT",FACE,{"disambiguationData":[TD([[makeQuery(id+"F0.imprint","IMPRINT",EDGE,{"derivedFrom":sQuery(id+"F0.wireOp",EDGE,"E131")}),1.0]])]});
            var Q40;
            Q40=makeQuery(id+"F0.imprint","IMPRINT",FACE,{"disambiguationData":[TD([[makeQuery(id+"F0.imprint","IMPRINT",EDGE,{"derivedFrom":sQuery(id+"F0.wireOp",EDGE,"E121")}),1.0]])]});
            var Q41;
            Q41=makeQuery(id+"F0.imprint","IMPRINT",FACE,{"disambiguationData":[TD([[makeQuery(id+"F0.imprint","IMPRINT",EDGE,{"derivedFrom":sQuery(id+"F0.wireOp",EDGE,"E111")}),1.0]])]});
            var Q42;
            Q42=makeQuery(id+"F0.imprint","IMPRINT",FACE,{"disambiguationData":[TD([[makeQuery(id+"F0.imprint","IMPRINT",EDGE,{"derivedFrom":sQuery(id+"F0.wireOp",EDGE,"E107")}),-1.0]])]});
            var Q43;
            Q43=makeQuery(id+"F0.imprint","IMPRINT",FACE,{"disambiguationData":[TD([[makeQuery(id+"F0.imprint","IMPRINT",EDGE,{"derivedFrom":sQuery(id+"F0.wireOp",EDGE,"E103")}),1.0]])]});
            var Q44;
            Q44=makeQuery(id+"F0.imprint","IMPRINT",FACE,{"disambiguationData":[TD([[makeQuery(id+"F0.imprint","IMPRINT",EDGE,{"derivedFrom":sQuery(id+"F0.wireOp",EDGE,"E93")}),1.0]])]});
            var Q45;
            Q45=makeQuery(id+"F0.imprint","IMPRINT",FACE,{"disambiguationData":[TD([[makeQuery(id+"F0.imprint","IMPRINT",EDGE,{"derivedFrom":sQuery(id+"F0.wireOp",EDGE,"E203")}),1.0]])]});
            var Q46;
            Q46=makeQuery(id+"F0.imprint","IMPRINT",FACE,{"disambiguationData":[TD([[makeQuery(id+"F0.imprint","IMPRINT",EDGE,{"derivedFrom":sQuery(id+"F0.wireOp",EDGE,"E205")}),1.0]])]});
            extrude(context, id + "F1", {"entities" : qUnion([Q0, Q1, Q2, Q3, Q4, Q5, Q6, Q7, Q8, Q9, Q10, Q11, Q12, Q13, Q14, Q15, Q16, Q17, Q18, Q19, Q20, Q21, Q22, Q23, Q24, Q25, Q26, Q27, Q28, Q29, Q30, Q31, Q32, Q33, Q34, Q35, Q36, Q37, Q38, Q39, Q40, Q41, Q42, Q43, Q44, Q45, Q46]), "depth" : 6.35 * mm, "offsetDistance" : 25.4 * mm});
        }
        {
            var Q0;
            Q0=makeQuery(id+"F0.imprint","IMPRINT",FACE,{"disambiguationData":[TD([[makeQuery(id+"F0.imprint","IMPRINT",EDGE,{"derivedFrom":sQuery(id+"F0.wireOp",EDGE,"E1")}),1.0]])]});
            var Q1;
            Q1=makeQuery(id+"F0.imprint","IMPRINT",FACE,{"disambiguationData":[TD([[makeQuery(id+"F0.imprint","IMPRINT",EDGE,{"derivedFrom":sQuery(id+"F0.wireOp",EDGE,"E205")}),-1.0]])]});
            var Q2;
            Q2=makeQuery(id+"F0.imprint","IMPRINT",FACE,{"disambiguationData":[TD([[makeQuery(id+"F0.imprint","IMPRINT",EDGE,{"derivedFrom":sQuery(id+"F0.wireOp",EDGE,"E177")}),1.0]])]});
            var Q3;
            Q3=makeQuery(id+"F0.imprint","IMPRINT",FACE,{"disambiguationData":[TD([[makeQuery(id+"F0.imprint","IMPRINT",EDGE,{"derivedFrom":sQuery(id+"F0.wireOp",EDGE,"E179")}),1.0]])]});
            var Q4;
            Q4=makeQuery(id+"F0.imprint","IMPRINT",FACE,{"disambiguationData":[TD([[makeQuery(id+"F0.imprint","IMPRINT",EDGE,{"derivedFrom":sQuery(id+"F0.wireOp",EDGE,"E155")}),1.0]])]});
            var Q5;
            Q5=makeQuery(id+"F0.imprint","IMPRINT",FACE,{"disambiguationData":[TD([[makeQuery(id+"F0.imprint","IMPRINT",EDGE,{"derivedFrom":sQuery(id+"F0.wireOp",EDGE,"E159")}),-1.0]])]});
            var Q6;
            Q6=makeQuery(id+"F0.imprint","IMPRINT",FACE,{"disambiguationData":[TD([[makeQuery(id+"F0.imprint","IMPRINT",EDGE,{"derivedFrom":sQuery(id+"F0.wireOp",EDGE,"E25")}),-1.0]])]});
            var Q7;
            Q7=makeQuery(id+"F0.imprint","IMPRINT",FACE,{"disambiguationData":[TD([[makeQuery(id+"F0.imprint","IMPRINT",EDGE,{"derivedFrom":sQuery(id+"F0.wireOp",EDGE,"E32")}),1.0]])]});
            var Q8;
            Q8=makeQuery(id+"F0.imprint","IMPRINT",FACE,{"disambiguationData":[TD([[makeQuery(id+"F0.imprint","IMPRINT",EDGE,{"derivedFrom":sQuery(id+"F0.wireOp",EDGE,"E40")}),1.0]])]});
            var Q9;
            Q9=makeQuery(id+"F0.imprint","IMPRINT",FACE,{"disambiguationData":[TD([[makeQuery(id+"F0.imprint","IMPRINT",EDGE,{"derivedFrom":sQuery(id+"F0.wireOp",EDGE,"E41")}),1.0]])]});
            var Q10;
            Q10=makeQuery(id+"F0.imprint","IMPRINT",FACE,{"disambiguationData":[TD([[makeQuery(id+"F0.imprint","IMPRINT",EDGE,{"derivedFrom":sQuery(id+"F0.wireOp",EDGE,"E109")}),-1.0]])]});
            extrude(context, id + "F2", {"entities" : qUnion([Q0, Q1, Q2, Q3, Q4, Q5, Q6, Q7, Q8, Q9, Q10]), "operationType" : NewBodyOperationType.ADD, "depth" : 5.08 * mm, "offsetDistance" : 25.4 * mm});
        }
        {
            var Q0;
            {var subQ0=sQuery(id+"F0.wireOp",EDGE,"E307");Q0=makeQuery(id+"F0.imprint","IMPRINT",FACE,{"disambiguationData":[TD([[makeQuery(id+"F0.imprint","IMPRINT",EDGE,{"derivedFrom":subQ0}),1.0]])]});}
            extrude(context, id + "F3", {"entities" : qUnion([Q0]), "operationType" : NewBodyOperationType.ADD, "depth" : 5.08 * mm, "offsetDistance" : 25.4 * mm});
        }
        {
            var Q0;
            Q0=sQuery(id+"F0.wireOp",VERTEX,"E308");
            var Q1;
            Q1=makeQuery(id+"F1.opExtrude","SWEPT_BODY",BODY,{"disambiguationData":[OSD([sQuery(id+"F0.wireOp",EDGE,"E1"),sQuery(id+"F0.wireOp",EDGE,"E2"),sQuery(id+"F0.wireOp",EDGE,"E3"),sQuery(id+"F0.wireOp",EDGE,"E4"),sQuery(id+"F0.wireOp",EDGE,"E5"),sQuery(id+"F0.wireOp",EDGE,"E6"),sQuery(id+"F0.wireOp",EDGE,"E7"),sQuery(id+"F0.wireOp",EDGE,"E8")])]});
            hole(context, id + "F4", {"style" : HoleStyle.SIMPLE, "endStyle" : HoleEndStyle.THROUGH, "oppositeDirection" : true, "holeDiameter" : 6.35 * mm, "majorDiameter" : 6.35 * mm, "isTappedThrough" : true, "tappedDepth" : 12.7 * mm, "tapClearance" : 3, "locations" : qUnion([Q0]), "scope" : qUnion([Q1])});
        }
    });
